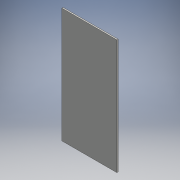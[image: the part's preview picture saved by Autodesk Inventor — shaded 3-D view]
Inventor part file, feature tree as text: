
AUTODESK INVENTOR PART (.ipt)
format: ipt  version: 2016 (Build 200138000, 138)  size: 90,112 bytes
history: native  units: mm
features: extrude x1, sketch x1
ambient origin geometry x8: Origin, YZ Plane, XZ Plane, XY Plane, X Axis, Y Axis, Z Axis, Center Point
bodies: Solid1 (feature_tree)
feature tree (2):
  extrude  "Extrusion1"  Depth=220.0mm
  sketch  "Sketch1"  dims[d0=460.0mm d1=220.0mm d2=5.0mm d3=0.0mm]
